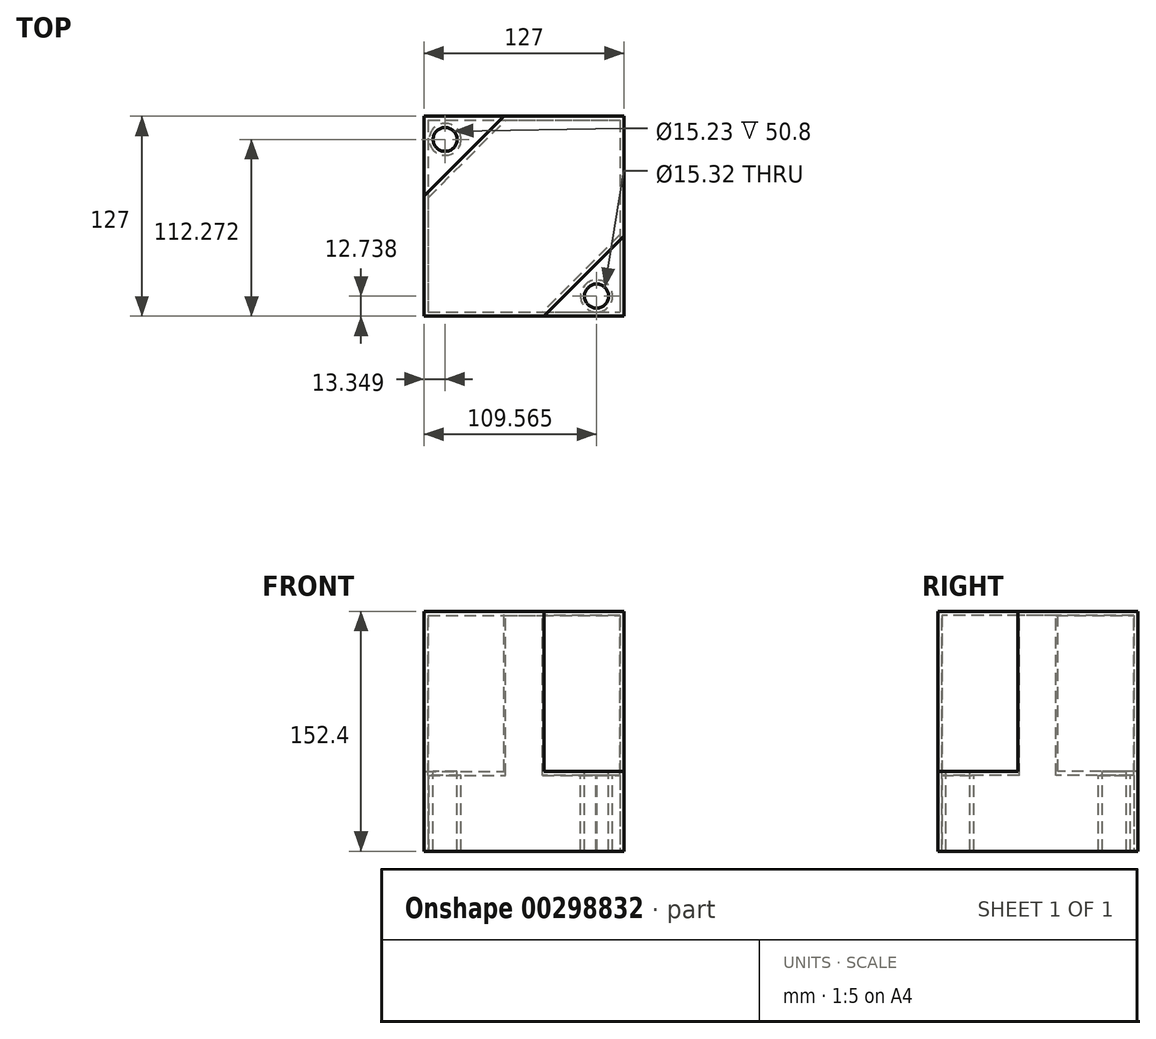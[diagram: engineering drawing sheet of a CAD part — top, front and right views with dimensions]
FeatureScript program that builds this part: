
annotation { "Feature Type Name" : "Feature", "Feature Type Description" : "" }
export const myFeature = defineFeature(function(context is Context, id is Id, definition is map)
    precondition{}
    {
        {
            var Q0;
            Q0=qCreatedBy(makeId("Top.planeOp"),FACE);
            var sketch = newSketch(context, id + "F0", { "sketchPlane" : qUnion([Q0])});
            skLineSegment(sketch, "E0.bottom", {"start": v(-59.16, 61.05) * mm, "end": v(67.84, 61.05) * mm});
            skLineSegment(sketch, "E0.top", {"start": v(-59.16, -65.95) * mm, "end": v(67.84, -65.95) * mm});
            skLineSegment(sketch, "E0.left", {"start": v(-59.16, 61.05) * mm, "end": v(-59.16, -65.95) * mm});
            skLineSegment(sketch, "E0.right", {"start": v(67.84, 61.05) * mm, "end": v(67.84, -65.95) * mm});
            skSolve(sketch);
        }
        {
            var Q0;
            Q0=makeQuery(id+"F0.imprint","IMPRINT",FACE,{"disambiguationData":[TD([[makeQuery(id+"F0.imprint","IMPRINT",EDGE,{"derivedFrom":sQuery(id+"F0.wireOp",EDGE,"E0.bottom")}),-1.0]])]});
            extrude(context, id + "F1", {"entities" : qUnion([Q0]), "depth" : 152.4 * mm});
        }
        {
            var Q0;
            Q0=makeQuery(id+"F1.opExtrude","CAP_FACE",FACE,{"disambiguationData":[OSD([sQuery(id+"F0.wireOp",EDGE,"E0.bottom"),sQuery(id+"F0.wireOp",EDGE,"E0.top"),sQuery(id+"F0.wireOp",EDGE,"E0.left"),sQuery(id+"F0.wireOp",EDGE,"E0.right")])],"isStart":false});
            var sketch = newSketch(context, id + "F2", { "sketchPlane" : qUnion([Q0])});
            skLineSegment(sketch, "E1", {"start": v(-59.16, 61.05) * mm, "end": v(-59.16, 10.25) * mm});
            skLineSegment(sketch, "E2", {"start": v(-59.16, 10.25) * mm, "end": v(-8.36, 61.05) * mm});
            skLineSegment(sketch, "E3", {"start": v(-8.36, 61.05) * mm, "end": v(-59.16, 61.05) * mm});
            skLineSegment(sketch, "E4", {"start": v(67.84, -65.95) * mm, "end": v(67.84, -15.15) * mm});
            skLineSegment(sketch, "E5", {"start": v(67.84, -15.15) * mm, "end": v(17.04, -65.95) * mm});
            skLineSegment(sketch, "E6", {"start": v(17.04, -65.95) * mm, "end": v(67.84, -65.95) * mm});
            skSolve(sketch);
        }
        {
            var Q0;
            Q0=makeQuery(id+"F2.imprint","IMPRINT",FACE,{"disambiguationData":[TD([[makeQuery(id+"F2.imprint","IMPRINT",EDGE,{"derivedFrom":sQuery(id+"F2.wireOp",EDGE,"E1")}),1.0]])]});
            var Q1;
            Q1=makeQuery(id+"F2.imprint","IMPRINT",FACE,{"disambiguationData":[TD([[makeQuery(id+"F2.imprint","IMPRINT",EDGE,{"derivedFrom":sQuery(id+"F2.wireOp",EDGE,"E4")}),-1.0]])]});
            extrude(context, id + "F3", {"entities" : qUnion([Q0, Q1]), "operationType" : NewBodyOperationType.REMOVE, "oppositeDirection" : true, "depth" : 101.6 * mm});
        }
        {
            var Q0;
            Q0=makeQuery(id+"F3.boolean.opBoolean","COPY",FACE,{"derivedFrom":makeQuery(id+"F3.opExtrude","CAP_FACE",FACE,{"disambiguationData":[OSD([sQuery(id+"F2.wireOp",EDGE,"E1"),sQuery(id+"F2.wireOp",EDGE,"E2"),sQuery(id+"F2.wireOp",EDGE,"E3")])],"isStart":false})});
            var sketch = newSketch(context, id + "F4", { "sketchPlane" : qUnion([Q0])});
            skCircle(sketch, "E7", {"center": v(-45.81, 46.32) * mm, "radius": 7.61 * mm});
            skCircle(sketch, "E8", {"center": v(50.4, -53.21) * mm, "radius": 7.66 * mm});
            skSolve(sketch);
        }
        {
            var Q0;
            Q0=makeQuery(id+"F4.imprint","IMPRINT",FACE,{"disambiguationData":[TD([[makeQuery(id+"F4.imprint","IMPRINT",EDGE,{"derivedFrom":sQuery(id+"F4.wireOp",EDGE,"E7")}),1.0]])]});
            var Q1;
            Q1=makeQuery(id+"F4.imprint","IMPRINT",FACE,{"disambiguationData":[TD([[makeQuery(id+"F4.imprint","IMPRINT",EDGE,{"derivedFrom":sQuery(id+"F4.wireOp",EDGE,"E8")}),1.0]])]});
            extrude(context, id + "F5", {"entities" : qUnion([Q0, Q1]), "operationType" : NewBodyOperationType.REMOVE, "oppositeDirection" : true, "depth" : 203.2 * mm});
        }
        {
            var Q0;
            Q0=makeQuery(id+"F1.opExtrude","CAP_FACE",FACE,{"disambiguationData":[OSD([sQuery(id+"F0.wireOp",EDGE,"E0.bottom"),sQuery(id+"F0.wireOp",EDGE,"E0.top"),sQuery(id+"F0.wireOp",EDGE,"E0.left"),sQuery(id+"F0.wireOp",EDGE,"E0.right")])],"isStart":true});
            shell(context, id + "F6", {"entities" : qUnion([Q0]), "thickness" : 2.54 * mm});
        }
    });
